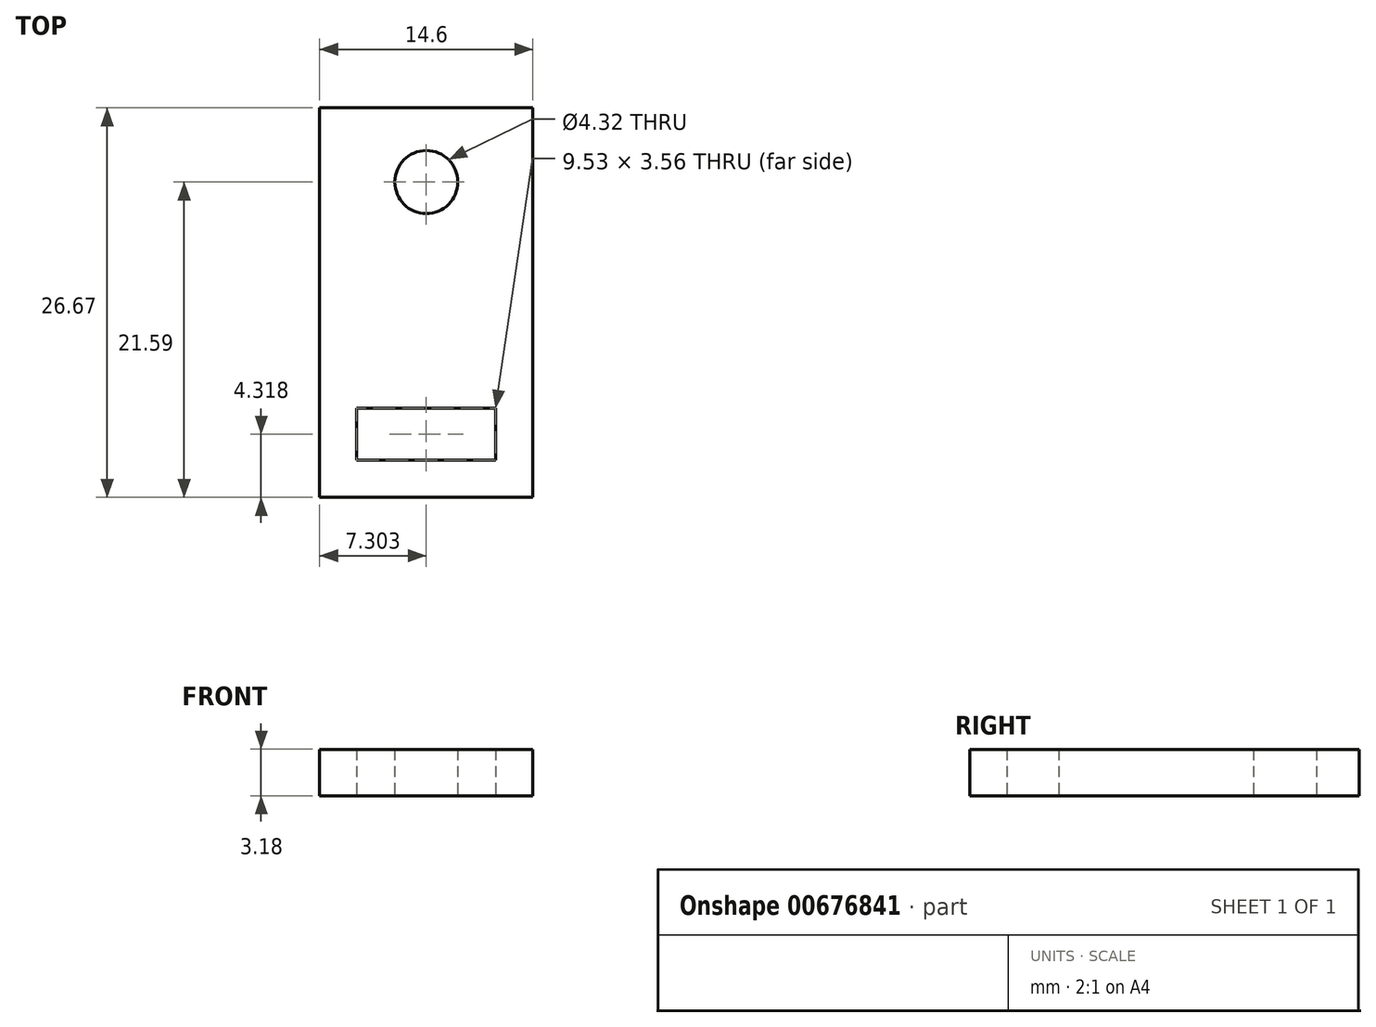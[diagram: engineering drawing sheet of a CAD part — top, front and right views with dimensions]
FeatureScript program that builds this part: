
annotation { "Feature Type Name" : "Feature", "Feature Type Description" : "" }
export const myFeature = defineFeature(function(context is Context, id is Id, definition is map)
    precondition{}
    {
        {
            var Q0;
            Q0=qCreatedBy(makeId("Top.planeOp"),FACE);
            var sketch = newSketch(context, id + "F0", { "sketchPlane" : qUnion([Q0])});
            skLineSegment(sketch, "E0.bottom", {"start": v(0, 0) * mm, "end": v(9.53, 0) * mm});
            skLineSegment(sketch, "E0.top", {"start": v(0, -21.59) * mm, "end": v(9.53, -21.59) * mm});
            skLineSegment(sketch, "E0.left", {"start": v(0, 0) * mm, "end": v(0, -21.59) * mm});
            skLineSegment(sketch, "E0.right", {"start": v(9.53, 0) * mm, "end": v(9.53, -21.59) * mm});
            skCircle(sketch, "E1", {"center": v(4.76, -2.54) * mm, "radius": 2.16 * mm});
            skLineSegment(sketch, "E2.top", {"start": v(0, -18.03) * mm, "end": v(9.53, -18.03) * mm});
            skLineSegment(sketch, "E2.left", {"start": v(0, -21.59) * mm, "end": v(0, -18.03) * mm});
            skLineSegment(sketch, "E2.right", {"start": v(9.53, -21.59) * mm, "end": v(9.53, -18.03) * mm});
            skLineSegment(sketch, "E3.bottom", {"start": v(0, 0) * mm, "end": v(-2.54, 0) * mm});
            skLineSegment(sketch, "E3.top", {"start": v(0, -21.59) * mm, "end": v(-2.54, -21.59) * mm});
            skLineSegment(sketch, "E3.right", {"start": v(-2.54, 0) * mm, "end": v(-2.54, -21.59) * mm});
            skLineSegment(sketch, "E4.bottom", {"start": v(9.53, 0) * mm, "end": v(12.07, 0) * mm});
            skLineSegment(sketch, "E4.top", {"start": v(9.53, -21.59) * mm, "end": v(12.07, -21.59) * mm});
            skLineSegment(sketch, "E4.right", {"start": v(12.07, 0) * mm, "end": v(12.07, -21.59) * mm});
            skLineSegment(sketch, "E5.bottom", {"start": v(-2.54, 0) * mm, "end": v(12.07, 0) * mm});
            skLineSegment(sketch, "E5.top", {"start": v(-2.54, 2.54) * mm, "end": v(12.07, 2.54) * mm});
            skLineSegment(sketch, "E5.left", {"start": v(-2.54, 0) * mm, "end": v(-2.54, 2.54) * mm});
            skLineSegment(sketch, "E5.right", {"start": v(12.07, 0) * mm, "end": v(12.07, 2.54) * mm});
            skLineSegment(sketch, "E6.bottom", {"start": v(-2.54, -21.59) * mm, "end": v(12.07, -21.59) * mm});
            skLineSegment(sketch, "E6.top", {"start": v(-2.54, -24.13) * mm, "end": v(12.07, -24.13) * mm});
            skLineSegment(sketch, "E6.left", {"start": v(-2.54, -21.59) * mm, "end": v(-2.54, -24.13) * mm});
            skLineSegment(sketch, "E6.right", {"start": v(12.07, -21.59) * mm, "end": v(12.07, -24.13) * mm});
            skSolve(sketch);
        }
        {
            var Q0;
            Q0=makeQuery(id+"F0.imprint","IMPRINT",FACE,{"disambiguationData":[TD([[makeQuery(id+"F0.imprint","IMPRINT",EDGE,{"derivedFrom":sQuery(id+"F0.wireOp",EDGE,"E1")}),-1.0]])]});
            var Q1;
            {var subQ0=sQuery(id+"F0.wireOp",EDGE,"E3.right");Q1=makeQuery(id+"F0.imprint","IMPRINT",FACE,{"disambiguationData":[TD([[makeQuery(id+"F0.imprint","IMPRINT",EDGE,{"derivedFrom":subQ0}),1.0]])]});}
            var Q2;
            {var subQ0=sQuery(id+"F0.wireOp",EDGE,"E4.right");Q2=makeQuery(id+"F0.imprint","IMPRINT",FACE,{"disambiguationData":[TD([[makeQuery(id+"F0.imprint","IMPRINT",EDGE,{"derivedFrom":subQ0}),-1.0]])]});}
            var Q3;
            Q3=makeQuery(id+"F0.imprint","IMPRINT",FACE,{"disambiguationData":[TD([[makeQuery(id+"F0.imprint","IMPRINT",EDGE,{"derivedFrom":sQuery(id+"F0.wireOp",EDGE,"E5.top")}),-1.0]])]});
            var Q4;
            Q4=makeQuery(id+"F0.imprint","IMPRINT",FACE,{"disambiguationData":[TD([[makeQuery(id+"F0.imprint","IMPRINT",EDGE,{"derivedFrom":sQuery(id+"F0.wireOp",EDGE,"E6.top")}),1.0]])]});
            extrude(context, id + "F1", {"entities" : qUnion([Q0, Q1, Q2, Q3, Q4]), "depth" : 3.17 * mm, "offsetDistance" : 25.4 * mm});
        }
    });
